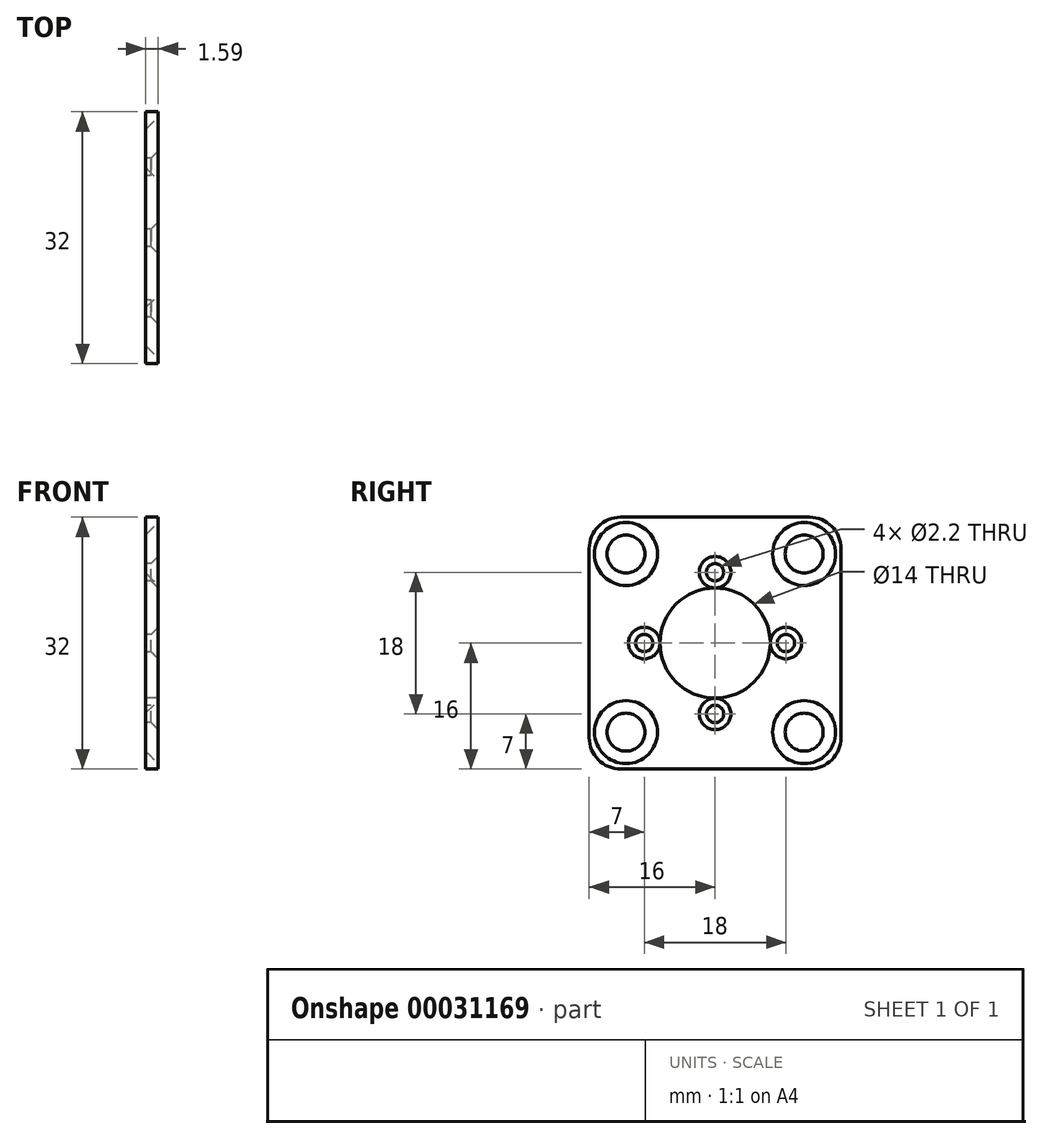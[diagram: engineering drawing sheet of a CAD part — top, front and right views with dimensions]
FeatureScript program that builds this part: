
annotation { "Feature Type Name" : "Feature", "Feature Type Description" : "" }
export const myFeature = defineFeature(function(context is Context, id is Id, definition is map)
    precondition{}
    {
        {
            var Q0;
            Q0=qCreatedBy(makeId("Right.planeOp"),FACE);
            var sketch = newSketch(context, id + "F0", { "sketchPlane" : qUnion([Q0])});
            skCircle(sketch, "E0", {"center": v(0, 0) * mm, "radius": 7 * mm});
            skCircle(sketch, "E1", {"center": v(0, 0) * mm, "radius": 9 * mm, "construction": true});
            skLineSegment(sketch, "E2.rect.bottom", {"start": v(16, 16) * mm, "end": v(-16, 16) * mm});
            skLineSegment(sketch, "E2.rect.top", {"start": v(16, -16) * mm, "end": v(-16, -16) * mm});
            skLineSegment(sketch, "E2.rect.left", {"start": v(16, 16) * mm, "end": v(16, -16) * mm});
            skLineSegment(sketch, "E2.rect.right", {"start": v(-16, 16) * mm, "end": v(-16, -16) * mm});
            skCircle(sketch, "E3", {"center": v(0, 0) * mm, "radius": 11 * mm, "construction": true});
            skCircle(sketch, "E4", {"center": v(0, 9) * mm, "radius": 1.1 * mm});
            skCircle(sketch, "E5", {"center": v(9, 0) * mm, "radius": 1.1 * mm});
            skCircle(sketch, "E6", {"center": v(0, -9) * mm, "radius": 1.1 * mm});
            skCircle(sketch, "E7", {"center": v(-9, 0) * mm, "radius": 1.1 * mm});
            skCircle(sketch, "E8", {"center": v(0, 0) * mm, "radius": 16 * mm, "construction": true});
            skCircle(sketch, "E9", {"center": v(-11.31, 11.31) * mm, "radius": 4 * mm, "construction": true});
            skCircle(sketch, "E10", {"center": v(11.31, 11.31) * mm, "radius": 2 * mm});
            skCircle(sketch, "E11", {"center": v(11.31, -11.31) * mm, "radius": 2 * mm});
            skCircle(sketch, "E12", {"center": v(-11.31, -11.31) * mm, "radius": 2 * mm});
            skCircle(sketch, "E13", {"center": v(-11.31, 11.31) * mm, "radius": 2 * mm});
            skLineSegment(sketch, "E14", {"start": v(-11.31, 11.31) * mm, "end": v(11.31, 11.31) * mm, "construction": true});
            skLineSegment(sketch, "E15", {"start": v(-11.31, -11.31) * mm, "end": v(-11.31, 11.31) * mm, "construction": true});
            skSolve(sketch);
        }
        {
            var Q0;
            Q0 = qSketchRegion(id + "F0", true);
            extrude(context, id + "F1", {"entities" : qUnion([Q0]), "depth" : 1.59 * mm});
        }
        {
            var Q0;
            Q0=makeQuery(id+"F1.opExtrude","CAP_FACE",FACE,{"disambiguationData":[OSD([sQuery(id+"F0.wireOp",EDGE,"E0"),sQuery(id+"F0.wireOp",EDGE,"E2.rect.bottom"),sQuery(id+"F0.wireOp",EDGE,"E2.rect.top"),sQuery(id+"F0.wireOp",EDGE,"E2.rect.left"),sQuery(id+"F0.wireOp",EDGE,"E2.rect.right"),sQuery(id+"F0.wireOp",EDGE,"E4"),sQuery(id+"F0.wireOp",EDGE,"E5"),sQuery(id+"F0.wireOp",EDGE,"E6"),sQuery(id+"F0.wireOp",EDGE,"E7"),sQuery(id+"F0.wireOp",EDGE,"E10"),sQuery(id+"F0.wireOp",EDGE,"E11"),sQuery(id+"F0.wireOp",EDGE,"E12"),sQuery(id+"F0.wireOp",EDGE,"E13")])],"isStart":false});
            var sketch = newSketch(context, id + "F2", { "sketchPlane" : qUnion([Q0])});
            skPoint(sketch, "E16", {"position": v(-11.31, 11.31) * mm});
            skPoint(sketch, "E17", {"position": v(11.31, 11.31) * mm});
            skPoint(sketch, "E18", {"position": v(11.31, -11.31) * mm});
            skPoint(sketch, "E19", {"position": v(-11.31, -11.31) * mm});
            skPoint(sketch, "E20", {"position": v(-9, 0) * mm});
            skPoint(sketch, "E21", {"position": v(0, 9) * mm});
            skPoint(sketch, "E22", {"position": v(9, 0) * mm});
            skPoint(sketch, "E23", {"position": v(0, -9) * mm});
            skSolve(sketch);
        }
        {
            var Q0;
            Q0=sQuery(id+"F2.wireOp",VERTEX,"E16");
            var Q1;
            Q1=sQuery(id+"F2.wireOp",VERTEX,"E17");
            var Q2;
            Q2=sQuery(id+"F2.wireOp",VERTEX,"E18");
            var Q3;
            Q3=sQuery(id+"F2.wireOp",VERTEX,"E19");
            var Q4;
            Q4=makeQuery(id+"F1.opExtrude","SWEPT_BODY",BODY,{"disambiguationData":[OSD([sQuery(id+"F0.wireOp",EDGE,"E0"),sQuery(id+"F0.wireOp",EDGE,"E2.rect.bottom"),sQuery(id+"F0.wireOp",EDGE,"E2.rect.top"),sQuery(id+"F0.wireOp",EDGE,"E2.rect.left"),sQuery(id+"F0.wireOp",EDGE,"E2.rect.right"),sQuery(id+"F0.wireOp",EDGE,"E4"),sQuery(id+"F0.wireOp",EDGE,"E5"),sQuery(id+"F0.wireOp",EDGE,"E6"),sQuery(id+"F0.wireOp",EDGE,"E7"),sQuery(id+"F0.wireOp",EDGE,"E10"),sQuery(id+"F0.wireOp",EDGE,"E11"),sQuery(id+"F0.wireOp",EDGE,"E12"),sQuery(id+"F0.wireOp",EDGE,"E13")])]});
            hole(context, id + "F3", {"style" : HoleStyle.C_SINK, "holeDiameter" : 4 * mm, "cSinkDiameter" : 8 * mm, "endStyle" : HoleEndStyle.THROUGH, "locations" : qUnion([Q0, Q1, Q2, Q3]), "scope" : qUnion([Q4]), "cSinkAngle" : 90 * degree});
        }
        {
            var Q0;
            Q0=sQuery(id+"F2.wireOp",VERTEX,"E20");
            var Q1;
            Q1=sQuery(id+"F2.wireOp",VERTEX,"E21");
            var Q2;
            Q2=sQuery(id+"F2.wireOp",VERTEX,"E22");
            var Q3;
            Q3=sQuery(id+"F2.wireOp",VERTEX,"E23");
            var Q4;
            Q4=makeQuery(id+"F1.opExtrude","SWEPT_BODY",BODY,{"disambiguationData":[OSD([sQuery(id+"F0.wireOp",EDGE,"E0"),sQuery(id+"F0.wireOp",EDGE,"E2.rect.bottom"),sQuery(id+"F0.wireOp",EDGE,"E2.rect.top"),sQuery(id+"F0.wireOp",EDGE,"E2.rect.left"),sQuery(id+"F0.wireOp",EDGE,"E2.rect.right"),sQuery(id+"F0.wireOp",EDGE,"E4"),sQuery(id+"F0.wireOp",EDGE,"E5"),sQuery(id+"F0.wireOp",EDGE,"E6"),sQuery(id+"F0.wireOp",EDGE,"E7"),sQuery(id+"F0.wireOp",EDGE,"E10"),sQuery(id+"F0.wireOp",EDGE,"E11"),sQuery(id+"F0.wireOp",EDGE,"E12"),sQuery(id+"F0.wireOp",EDGE,"E13")])]});
            hole(context, id + "F4", {"style" : HoleStyle.C_SINK, "holeDiameter" : 2 * mm, "cSinkDiameter" : 4 * mm, "endStyle" : HoleEndStyle.THROUGH, "locations" : qUnion([Q0, Q1, Q2, Q3]), "scope" : qUnion([Q4]), "cSinkAngle" : 90 * degree});
        }
        {
            var Q0;
            Q0=makeQuery(id+"F1.opExtrude","SWEPT_EDGE",EDGE,{"disambiguationData":[OSD([sQuery(id+"F0.wireOp",EDGE,"E2.rect.bottom"),sQuery(id+"F0.wireOp",EDGE,"E2.rect.right")])]});
            var Q1;
            Q1=makeQuery(id+"F1.opExtrude","SWEPT_EDGE",EDGE,{"disambiguationData":[OSD([sQuery(id+"F0.wireOp",EDGE,"E2.rect.bottom"),sQuery(id+"F0.wireOp",EDGE,"E2.rect.left")])]});
            var Q2;
            Q2=makeQuery(id+"F1.opExtrude","SWEPT_EDGE",EDGE,{"disambiguationData":[OSD([sQuery(id+"F0.wireOp",EDGE,"E2.rect.top"),sQuery(id+"F0.wireOp",EDGE,"E2.rect.left")])]});
            var Q3;
            Q3=makeQuery(id+"F1.opExtrude","SWEPT_EDGE",EDGE,{"disambiguationData":[OSD([sQuery(id+"F0.wireOp",EDGE,"E2.rect.top"),sQuery(id+"F0.wireOp",EDGE,"E2.rect.right")])]});
            fillet(context, id + "F5", {"entities" : qUnion([Q0, Q1, Q2, Q3]), "radius" : 4 * mm, "tangentPropagation" : true, "allowEdgeOverflow" : false});
        }
    });
